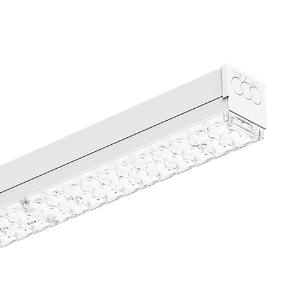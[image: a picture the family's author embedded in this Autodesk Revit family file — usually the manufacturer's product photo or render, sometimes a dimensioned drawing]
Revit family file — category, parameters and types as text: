
# Revit family: 3f_filippi_-_3f_zeta_l_ugr_3f_filippi_-_10842_-_3f_zeta_l_ugr_30-940_led_dali_l1194
name_source: partatom
category: Lighting Fixtures
units: mm (PartAtom-declared; Revit-internal decimal feet)

## family parameters
Cut with Voids When Loaded = No
Host = Face
Light Source = No
Part Type = Normal
Room Calculation Point = No
Round Connector Dimension = Use Diameter
Shared = No

## types (1)
- 3F Filippi - 3F Zeta L UGR (1 x LED, 4248 lm, 33 W, 4000 K)
    Apparent Load = 33 VA
    Approval mark = ENEC
    CIE Flux Codes = 83 96 99 97 100
    Color Rendering = 90
    Color Temperature = 4000 K
    Control Gear = Electronic transformer
    Default Elevation = 1800 mm
    Description = ILLUMINOTECHNICAL
Luminous efficiency 100% (DLOR 97%, ULOR 3%).
Initial luminous flux of the luminaire 4248 lm.
Controlled direct symmetric distribution.
Installation Interdistance Transv.D = 1.39 x hu - Long.D = 1.30 x hu.
Average luminance <3000 cd/m² for radial angles >65°.
Tabular UGR (CIE 117 - 4H-8H; S=0.25H; 70/50/20): RUG 18.3 - 16.7.
Beam angle: 78° - 75°.
Luminous efficacy 129 lm/W.
Lifetime (L93/B10): 30000 h. (tq+25°C)
Lifetime (L90/B10): 50000 h. (tq+25°C)
Lifetime (L85/B10): 80000 h. (tq+25°C)
Lifetime (L80/B10): 100000 h. (tq+25°C)
Sudden decreased luminous flux after 50000 hours: 0% (C0).
Photobiological safety in compliance with IEC/TR 62778: RG0 risk exempt, (IEC 62471).
In compliance with IEC/EN 62722-2-1 - IEC/EN 62717 standards.

SOURCE
Linear LED module 30W/940.
Energy efficiency class (UE 2019/2020 - UE 2019/2015): E.
CIE 13.3 Colour rendering index: CRI >90 (R9 >50%).
IES TM-30 Fidelity Index: Rf = 92 Rg = 101.
CCT nominal colour temperature 4000 K.
Colour initial tolerance (MacAdam): SDCM 3.

MECHANICAL
Housing in hot-galvanised steel, painted in white polyester, obtained through rolling process.
Light unit in hot-galvanised steel, painted in white polyester base with fixing springs and retractable safety hooks in stainless steel.
Transparent methacrylate (PMMA) controlled distribution lenses with flat external surface.
End caps in white polycarbonate.
Pair of stainless steel sliding brackets with sliding block screws.
Luminaire with limited surface temperature. - D - (EN 60598-2-24)
Dimensions: 1194x62 mm, height 65 mm. Weight 3.3 kg.
IP40 protection degree.
Mechanical strength to impacts IK06 (1 joule).
Glow-wire test resistance 650°C.

ELECTRICAL
Halogen Free DALI-2, PUSH-DIM, electronic wiring 230V-50/60Hz, power factor 0.90 at full load, THD <25%, constant output current, class I, 1 driver, 1 DALI addresse.
Power of the luminaire 33 W.
CE - IEC 60598-1 - EN 60598-1.
SAFE FLICKER: PstLM=<1 and SVM=<0.4 (IEC TR 61547-1 and IEC TR 63158), to ensure a more comfortable and safe light.
Luminaire compliant with EN 60598-2-22 for power supply from a centralised emergency system CPSS (Central Power Supply System), not incorporated in the luminaire - high risk areas excluded. The default power and flux are 100% in AC and 15% in DC.
Ambient temperature from 0°C to +25°C.
Temperature class T6 max 85°C.
Relative humidity UR: <85%.

INSTALLATION
Ceiling / Suspended / Wall.
All accessories dedicated to this product are available on the Catalog and on our website www.3F-Filippi.com.

APPLICATIONS
Suitable product for food production plants (HACCP), IFS (Food Version 6), BRC (GSFS Food Version 7).
In commercial environments, exhibition areas, shops and stores.
In environments with VDTs, managerial offices and staterooms, public offices and schools.

LIGHT MANAGEMENT
Recommended minimum setting: 10%.
The device, equipped with DALI-2 driver, can be controlled manually with 3F Easy Dim technology or automatically/manually with 3F Smart Dimming technology and/or centralised DALI systems.
DALI-2 certification guarantees interoperability with other devices with the same certification.
In electrical systems without a regulation system (manual or automatic) and DALI bus, a suitable jumper must be made on the DA-DA terminals of the appliance.

WARNING
Luminaire designed for disposal/recycling at end-of-life.
Replaceable (LED only) light source by a professional. Replaceable control gear by a professional.
    Height = 65 mm
    Lamp = 1 x LED
    Lamp Light Flux = 4248 lm
    Lamp Power = 33 W
    Lamp count = 1
    Length = 1194 mm
    Lifetime = 50000 h
    Luminous efficacy = 129 lm/W
    Manufacturer = 3F Filippi
    ModVariant = No
    Model = 3F Filippi - 10842 - 3F Zeta L UGR 30-940 LED DALI L1194
    Mounting Place = Ceiling
    Mounting Type = Surface mounted
    Number of Poles = 1
    OnlyDefault = Yes
    Power Factor = 1
    Product Name = 3F Filippi - 3F Zeta L UGR
    Product group = ceiling mounted luminaire
    ProductGroupID = 3
    Protection Class = Protection class I
    Protection Degree = IP 40
    RLX_Detail_Level = 1
    RLX_Emergency_Light_Flux = 0 lm
    RLX_Emergency_Type = 0
    RLX_Emergency_Type_DB = No
    RlxData = <blob elided: 50265 chars, md5=0a50de34>
    Socket = socket
    Standby Power = 0 W
    System Light Flux = 4248 lm
    System Power = 33 W
    Type Comments = Product without accessories
    Type Image = 3ffilippi_3f_zeta_l_ugr.jpg
    URL = http://relux.com
    VarID = ---
    Voltage = 0 V
    Weight = 0.00 kg
    Width = 62 mm  [stored 0.203412 ft]

note: [stored X ft] marks values corroborated as IEEE doubles in the binary element streams (Revit-internal decimal feet)

## geometry (parser evidence)
native form markers: Blend x4, Sweep x10
no freeform markers — native parametric forms only
